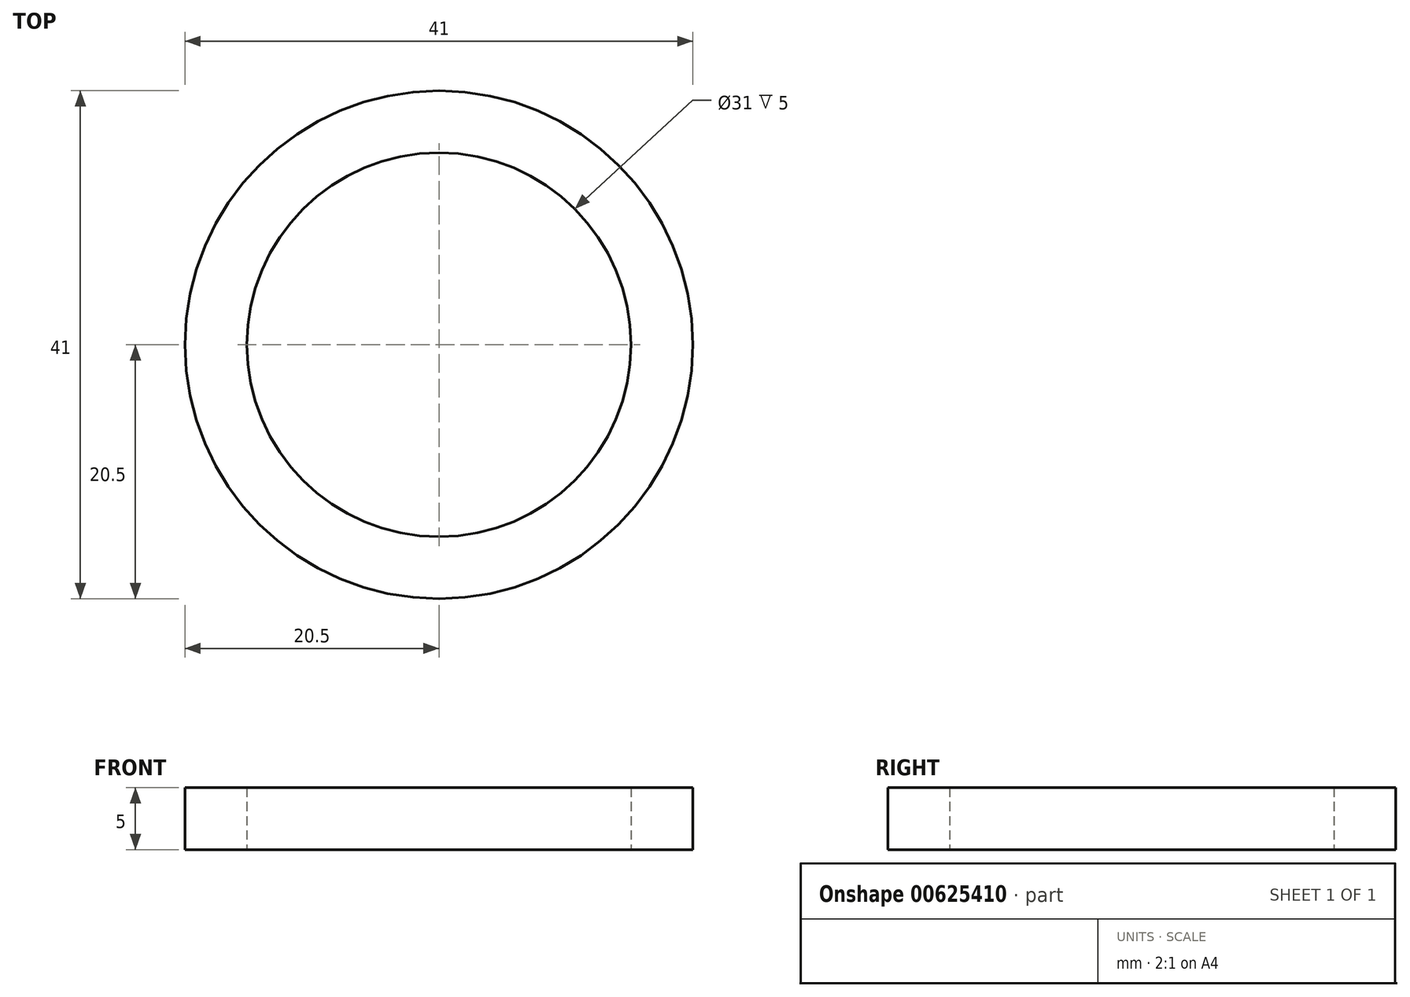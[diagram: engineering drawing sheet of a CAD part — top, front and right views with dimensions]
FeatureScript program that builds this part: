
annotation { "Feature Type Name" : "Feature", "Feature Type Description" : "" }
export const myFeature = defineFeature(function(context is Context, id is Id, definition is map)
    precondition{}
    {
        {
            var Q0;
            Q0=qCreatedBy(makeId("Top.planeOp"),FACE);
            var sketch = newSketch(context, id + "F0", { "sketchPlane" : qUnion([Q0])});
            skCircle(sketch, "E0", {"center": v(0, 0) * mm, "radius": 15.5 * mm});
            skCircle(sketch, "E1", {"center": v(0, 0) * mm, "radius": 20.5 * mm});
            skSolve(sketch);
        }
        {
            var Q0;
            Q0=makeQuery(id+"F0.imprint","IMPRINT",FACE,{"disambiguationData":[TD([[makeQuery(id+"F0.imprint","IMPRINT",EDGE,{"derivedFrom":sQuery(id+"F0.wireOp",EDGE,"E0")}),-1.0]])]});
            extrude(context, id + "F1", {"entities" : qUnion([Q0]), "depth" : 5 * mm, "offsetDistance" : 25 * mm});
        }
    });
